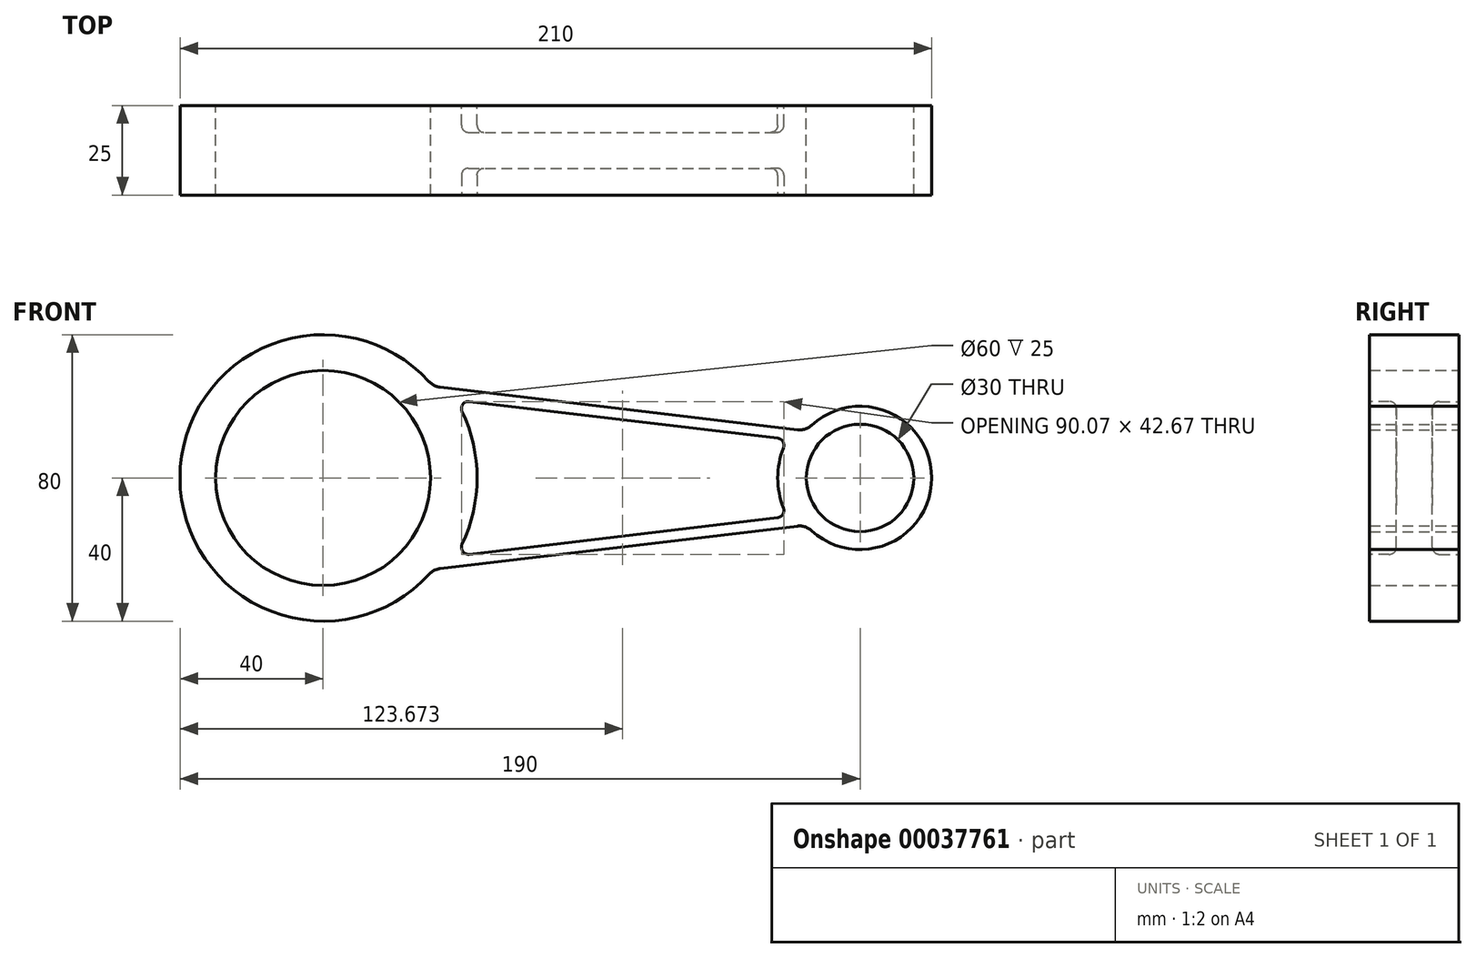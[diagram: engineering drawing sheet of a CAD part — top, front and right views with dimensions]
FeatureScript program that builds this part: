
annotation { "Feature Type Name" : "Feature", "Feature Type Description" : "" }
export const myFeature = defineFeature(function(context is Context, id is Id, definition is map)
    precondition{}
    {
        {
            var Q0;
            Q0=qCreatedBy(makeId("Front.planeOp"),FACE);
            var sketch = newSketch(context, id + "F0", { "sketchPlane" : qUnion([Q0])});
            skCircle(sketch, "E0", {"center": v(-75, 0) * mm, "radius": 40 * mm});
            skCircle(sketch, "E1", {"center": v(75, 0) * mm, "radius": 20 * mm});
            skLineSegment(sketch, "E2", {"start": v(-75, 0) * mm, "end": v(75, 0) * mm, "construction": true});
            skLineSegment(sketch, "E3", {"start": v(-44.23, 25.56) * mm, "end": v(59.94, 13.16) * mm});
            skLineSegment(sketch, "E4.MirrorCS", {"start": v(-44.23, -25.56) * mm, "end": v(59.94, -13.16) * mm});
            skPoint(sketch, "E5.orphan", {"position": v(-66.73, 28.23) * mm});
            skPoint(sketch, "E6.orphan", {"position": v(-66.73, -28.23) * mm});
            skPoint(sketch, "E7.orphan", {"position": v(74.03, -11.48) * mm});
            skPoint(sketch, "E8.orphan", {"position": v(74.03, 11.48) * mm});
            skSolve(sketch);
        }
        {
            var Q0;
            Q0 = qSketchRegion(id + "F0", true);
            extrude(context, id + "F1", {"entities" : qUnion([Q0]), "depth" : 25 / 2 * mm});
        }
        {
            var Q0;
            Q0=makeQuery(id+"F1.opExtrude","CAP_FACE",FACE,{"disambiguationData":[OSD([sQuery(id+"F0.wireOp",EDGE,"E0"),sQuery(id+"F0.wireOp",EDGE,"E1"),sQuery(id+"F0.wireOp",EDGE,"E3"),sQuery(id+"F0.wireOp",EDGE,"E4.MirrorCS")])],"isStart":false});
            var sketch = newSketch(context, id + "F2", { "sketchPlane" : qUnion([Q0])});
            skArc(sketch, "E9", {"start": v(-44.23, -25.56) * mm, "mid": v(-35, 0) * mm, "end": v(-44.23, 25.56) * mm});
            skArc(sketch, "E10", {"start": v(59.94, 13.16) * mm, "mid": v(55, 0) * mm, "end": v(59.94, -13.16) * mm});
            skPoint(sketch, "E11.0.end.orphan", {"position": v(59.94, 13.16) * mm});
            skPoint(sketch, "E11.0.start.orphan", {"position": v(59.94, -13.16) * mm});
            skPoint(sketch, "E12.0.end.orphan", {"position": v(-44.23, -25.56) * mm});
            skPoint(sketch, "E12.0.start.orphan", {"position": v(-44.23, 25.56) * mm});
            skLineSegment(sketch, "E13.0", {"start": v(-37.93, 21.78) * mm, "end": v(54.67, 10.76) * mm});
            skArc(sketch, "E13.1", {"start": v(-37.93, -21.78) * mm, "mid": v(-32, 0) * mm, "end": v(-37.93, 21.78) * mm});
            skLineSegment(sketch, "E13.2", {"start": v(-37.93, -21.78) * mm, "end": v(54.67, -10.76) * mm});
            skArc(sketch, "E13.3", {"start": v(54.67, 10.76) * mm, "mid": v(52, 0) * mm, "end": v(54.67, -10.76) * mm});
            skSolve(sketch);
        }
        {
            var Q0;
            Q0=makeQuery(id+"F2.imprint","IMPRINT",FACE,{"disambiguationData":[TD([[makeQuery(id+"F2.imprint","IMPRINT",EDGE,{"derivedFrom":sQuery(id+"F2.wireOp",EDGE,"E13.0")}),-1.0]])]});
            extrude(context, id + "F3", {"entities" : qUnion([Q0]), "operationType" : NewBodyOperationType.REMOVE, "oppositeDirection" : true, "depth" : 7.5 * mm});
        }
        {
            var Q0;
            Q0=makeQuery(id+"F3.boolean.opBoolean","COPY",EDGE,{"derivedFrom":makeQuery(id+"F3.opExtrude","SWEPT_EDGE",EDGE,{"disambiguationData":[OSD([sQuery(id+"F2.wireOp",EDGE,"E13.1"),sQuery(id+"F2.wireOp",EDGE,"E13.2")])]})});
            var Q1;
            Q1=makeQuery(id+"F3.boolean.opBoolean","COPY",EDGE,{"derivedFrom":makeQuery(id+"F3.opExtrude","SWEPT_EDGE",EDGE,{"disambiguationData":[OSD([sQuery(id+"F2.wireOp",EDGE,"E13.0"),sQuery(id+"F2.wireOp",EDGE,"E13.3")])]})});
            var Q2;
            Q2=makeQuery(id+"F3.boolean.opBoolean","COPY",EDGE,{"derivedFrom":makeQuery(id+"F3.opExtrude","SWEPT_EDGE",EDGE,{"disambiguationData":[OSD([sQuery(id+"F2.wireOp",EDGE,"E13.2"),sQuery(id+"F2.wireOp",EDGE,"E13.3")])]})});
            var Q3;
            Q3=makeQuery(id+"F3.boolean.opBoolean","COPY",EDGE,{"derivedFrom":makeQuery(id+"F3.opExtrude","SWEPT_EDGE",EDGE,{"disambiguationData":[OSD([sQuery(id+"F2.wireOp",EDGE,"E13.0"),sQuery(id+"F2.wireOp",EDGE,"E13.1")])]})});
            fillet(context, id + "F4", {"entities" : qUnion([Q0, Q1, Q2, Q3]), "radius" : 2 * mm, "tangentPropagation" : true, "allowEdgeOverflow" : false});
        }
        {
            var Q0;
            Q0=makeQuery(id+"F3.boolean.opBoolean","COPY",EDGE,{"derivedFrom":makeQuery(id+"F3.opExtrude","CAP_EDGE",EDGE,{"disambiguationData":[OSD([sQuery(id+"F2.wireOp",EDGE,"E13.0")])],"isStart":false})});
            fillet(context, id + "F5", {"entities" : qUnion([Q0]), "radius" : 2 * mm, "tangentPropagation" : true, "allowEdgeOverflow" : false});
        }
        {
            var Q0;
            Q0=makeQuery(id+"F1.opExtrude","SWEPT_BODY",BODY,{"disambiguationData":[OSD([sQuery(id+"F0.wireOp",EDGE,"E0"),sQuery(id+"F0.wireOp",EDGE,"E1"),sQuery(id+"F0.wireOp",EDGE,"E3"),sQuery(id+"F0.wireOp",EDGE,"E4.MirrorCS")])]});
            var Q1;
            Q1=qCreatedBy(makeId("Front.planeOp"),FACE);
            mirror(context, id + "F6", {"operationType" : NewBodyOperationType.ADD, "entities" : qUnion([Q0]), "mirrorPlane" : qUnion([Q1])});
        }
        {
            var Q0;
            Q0=makeQuery(id+"F1.opExtrude","CAP_FACE",FACE,{"disambiguationData":[OSD([sQuery(id+"F0.wireOp",EDGE,"E0"),sQuery(id+"F0.wireOp",EDGE,"E1"),sQuery(id+"F0.wireOp",EDGE,"E3"),sQuery(id+"F0.wireOp",EDGE,"E4.MirrorCS")])],"isStart":false});
            var sketch = newSketch(context, id + "F7", { "sketchPlane" : qUnion([Q0])});
            skArc(sketch, "E14.0", {"start": v(-44.23, 25.56) * mm, "mid": v(-115, 0) * mm, "end": v(-44.23, -25.56) * mm});
            skArc(sketch, "E15.0", {"start": v(59.94, -13.16) * mm, "mid": v(95, 0) * mm, "end": v(59.94, 13.16) * mm});
            skSolve(sketch);
        }
        {
            var Q0;
            Q0=sQuery(id+"F7.wireOp",VERTEX,"E14.0.center");
            var Q1;
            Q1=makeQuery(id+"F1.opExtrude","SWEPT_BODY",BODY,{"disambiguationData":[OSD([sQuery(id+"F0.wireOp",EDGE,"E0"),sQuery(id+"F0.wireOp",EDGE,"E1"),sQuery(id+"F0.wireOp",EDGE,"E3"),sQuery(id+"F0.wireOp",EDGE,"E4.MirrorCS")])]});
            hole(context, id + "F8", {"style" : HoleStyle.SIMPLE, "endStyle" : HoleEndStyle.THROUGH, "holeDiameter" : 60 * mm, "tappedDepth" : 12 * mm, "tapClearance" : 3, "locations" : qUnion([Q0]), "scope" : qUnion([Q1])});
        }
        {
            var Q0;
            Q0=sQuery(id+"F7.wireOp",VERTEX,"E15.0.center");
            var Q1;
            Q1=makeQuery(id+"F1.opExtrude","SWEPT_BODY",BODY,{"disambiguationData":[OSD([sQuery(id+"F0.wireOp",EDGE,"E0"),sQuery(id+"F0.wireOp",EDGE,"E1"),sQuery(id+"F0.wireOp",EDGE,"E3"),sQuery(id+"F0.wireOp",EDGE,"E4.MirrorCS")])]});
            hole(context, id + "F9", {"style" : HoleStyle.SIMPLE, "endStyle" : HoleEndStyle.THROUGH, "holeDiameter" : 30 * mm, "tappedDepth" : 12 * mm, "tapClearance" : 3, "locations" : qUnion([Q0]), "scope" : qUnion([Q1])});
        }
        {
            var Q0;
            {var subQ0=makeQuery(id+"F1.opExtrude","SWEPT_EDGE",EDGE,{"disambiguationData":[OSD([sQuery(id+"F0.wireOp",EDGE,"E0"),sQuery(id+"F0.wireOp",EDGE,"E3")])]});Q0=makeQuery(id+"F6.boolean.opBoolean","MERGE",EDGE,{"derivedFrom":[subQ0,makeQuery(id+"F6.opPattern","COPY",EDGE,{"derivedFrom":subQ0,"instanceName":"1"})]});}
            var Q1;
            {var subQ0=makeQuery(id+"F1.opExtrude","SWEPT_EDGE",EDGE,{"disambiguationData":[OSD([sQuery(id+"F0.wireOp",EDGE,"E1"),sQuery(id+"F0.wireOp",EDGE,"E3")])]});Q1=makeQuery(id+"F6.boolean.opBoolean","MERGE",EDGE,{"derivedFrom":[subQ0,makeQuery(id+"F6.opPattern","COPY",EDGE,{"derivedFrom":subQ0,"instanceName":"1"})]});}
            var Q2;
            {var subQ0=makeQuery(id+"F1.opExtrude","SWEPT_EDGE",EDGE,{"disambiguationData":[OSD([sQuery(id+"F0.wireOp",EDGE,"E0"),sQuery(id+"F0.wireOp",EDGE,"E4.MirrorCS")])]});Q2=makeQuery(id+"F6.boolean.opBoolean","MERGE",EDGE,{"derivedFrom":[subQ0,makeQuery(id+"F6.opPattern","COPY",EDGE,{"derivedFrom":subQ0,"instanceName":"1"})]});}
            var Q3;
            {var subQ0=makeQuery(id+"F1.opExtrude","SWEPT_EDGE",EDGE,{"disambiguationData":[OSD([sQuery(id+"F0.wireOp",EDGE,"E1"),sQuery(id+"F0.wireOp",EDGE,"E4.MirrorCS")])]});Q3=makeQuery(id+"F6.boolean.opBoolean","MERGE",EDGE,{"derivedFrom":[subQ0,makeQuery(id+"F6.opPattern","COPY",EDGE,{"derivedFrom":subQ0,"instanceName":"1"})]});}
            fillet(context, id + "F10", {"entities" : qUnion([Q0, Q1, Q2, Q3]), "radius" : 5 * mm, "tangentPropagation" : true, "allowEdgeOverflow" : false});
        }
    });
